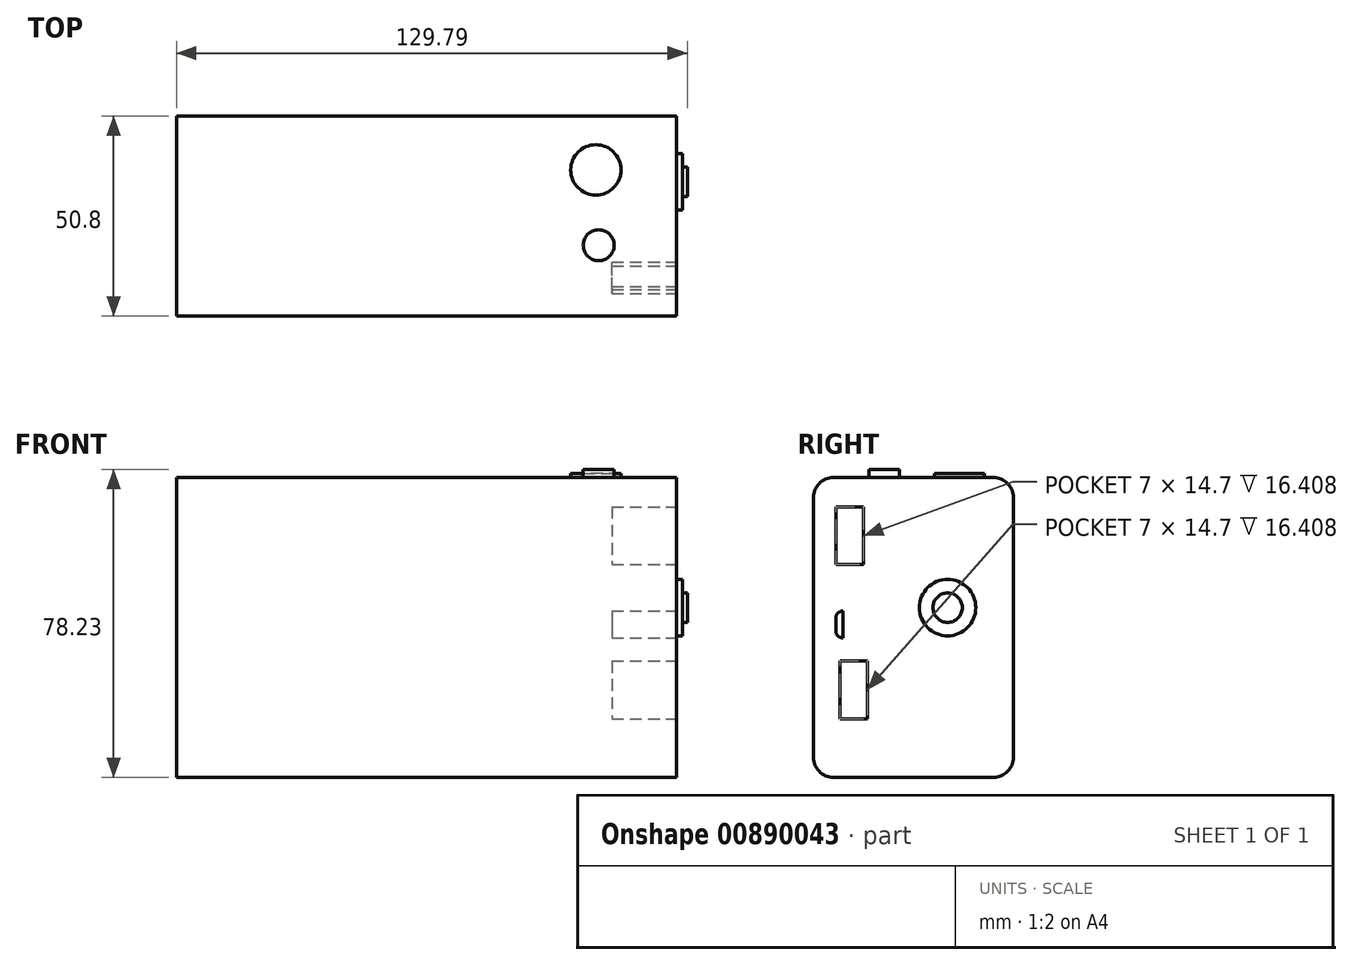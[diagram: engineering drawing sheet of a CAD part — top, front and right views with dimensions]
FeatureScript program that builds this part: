
annotation { "Feature Type Name" : "Feature", "Feature Type Description" : "" }
export const myFeature = defineFeature(function(context is Context, id is Id, definition is map)
    precondition{}
    {
        {
            var Q0;
            Q0=qCreatedBy(makeId("Front.planeOp"),FACE);
            var sketch = newSketch(context, id + "F0", { "sketchPlane" : qUnion([Q0])});
            skLineSegment(sketch, "E0.bottom", {"start": v(63.5, 38.1) * mm, "end": v(-63.5, 38.1) * mm});
            skLineSegment(sketch, "E0.top", {"start": v(63.5, -38.1) * mm, "end": v(-63.5, -38.1) * mm});
            skLineSegment(sketch, "E0.left", {"start": v(63.5, 38.1) * mm, "end": v(63.5, -38.1) * mm});
            skLineSegment(sketch, "E0.right", {"start": v(-63.5, 38.1) * mm, "end": v(-63.5, -38.1) * mm});
            skPoint(sketch, "E0.middle", {"position": v(0, 0) * mm});
            skSolve(sketch);
        }
        {
            var Q0;
            Q0=makeQuery(id+"F0.imprint","IMPRINT",FACE,{"disambiguationData":[TD([[makeQuery(id+"F0.imprint","IMPRINT",EDGE,{"derivedFrom":sQuery(id+"F0.wireOp",EDGE,"E0.bottom")}),1.0]])]});
            extrude(context, id + "F1", {"entities" : qUnion([Q0]), "depth" : 50.8 * mm, "offsetDistance" : 25.4 * mm});
        }
        {
            var Q0;
            Q0=makeQuery(id+"F1.opExtrude","CAP_EDGE",EDGE,{"disambiguationData":[OSD([sQuery(id+"F0.wireOp",EDGE,"E0.bottom")])],"isStart":false});
            var Q1;
            Q1=makeQuery(id+"F1.opExtrude","CAP_EDGE",EDGE,{"disambiguationData":[OSD([sQuery(id+"F0.wireOp",EDGE,"E0.top")])],"isStart":false});
            var Q2;
            Q2=makeQuery(id+"F1.opExtrude","CAP_EDGE",EDGE,{"disambiguationData":[OSD([sQuery(id+"F0.wireOp",EDGE,"E0.bottom")])],"isStart":true});
            var Q3;
            Q3=makeQuery(id+"F1.opExtrude","CAP_EDGE",EDGE,{"disambiguationData":[OSD([sQuery(id+"F0.wireOp",EDGE,"E0.top")])],"isStart":true});
            fillet(context, id + "F2", {"entities" : qUnion([Q0, Q1, Q2, Q3]), "radius" : 5.08 * mm, "tangentPropagation" : true, "allowEdgeOverflow" : false});
        }
        {
            var Q0;
            Q0=makeQuery(id+"F1.opExtrude","SWEPT_FACE",FACE,{"disambiguationData":[OSD([sQuery(id+"F0.wireOp",EDGE,"E0.left")])]});
            var sketch = newSketch(context, id + "F3", { "sketchPlane" : qUnion([Q0])});
            skLineSegment(sketch, "E1.bottom", {"start": v(-45.09, 30.66) * mm, "end": v(-38.09, 30.66) * mm});
            skLineSegment(sketch, "E1.top", {"start": v(-45.09, 15.96) * mm, "end": v(-38.09, 15.96) * mm});
            skLineSegment(sketch, "E1.left", {"start": v(-45.09, 30.66) * mm, "end": v(-45.09, 15.96) * mm});
            skLineSegment(sketch, "E1.right", {"start": v(-38.09, 30.66) * mm, "end": v(-38.09, 15.96) * mm});
            skSolve(sketch);
        }
        {
            var Q0;
            Q0=makeQuery(id+"F3.imprint","IMPRINT",FACE,{"disambiguationData":[TD([[makeQuery(id+"F3.imprint","IMPRINT",EDGE,{"derivedFrom":sQuery(id+"F3.wireOp",EDGE,"E1.bottom")}),-1.0]])]});
            extrude(context, id + "F4", {"entities" : qUnion([Q0]), "operationType" : NewBodyOperationType.REMOVE, "oppositeDirection" : true, "depth" : 16.4 * mm, "offsetDistance" : 25.4 * mm});
        }
        {
            var Q0;
            Q0=makeQuery(id+"F1.opExtrude","SWEPT_FACE",FACE,{"disambiguationData":[OSD([sQuery(id+"F0.wireOp",EDGE,"E0.left")])]});
            var sketch = newSketch(context, id + "F5", { "sketchPlane" : qUnion([Q0])});
            skLineSegment(sketch, "E2.bottom", {"start": v(-44.08, -8.52) * mm, "end": v(-37.08, -8.52) * mm});
            skLineSegment(sketch, "E2.top", {"start": v(-44.08, -23.22) * mm, "end": v(-37.08, -23.22) * mm});
            skLineSegment(sketch, "E2.left", {"start": v(-44.08, -8.52) * mm, "end": v(-44.08, -23.22) * mm});
            skLineSegment(sketch, "E2.right", {"start": v(-37.08, -8.52) * mm, "end": v(-37.08, -23.22) * mm});
            skSolve(sketch);
        }
        {
            var Q0;
            Q0=makeQuery(id+"F5.imprint","IMPRINT",FACE,{"disambiguationData":[TD([[makeQuery(id+"F5.imprint","IMPRINT",EDGE,{"derivedFrom":sQuery(id+"F5.wireOp",EDGE,"E2.bottom")}),-1.0]])]});
            extrude(context, id + "F6", {"entities" : qUnion([Q0]), "operationType" : NewBodyOperationType.REMOVE, "oppositeDirection" : true, "depth" : 16.4 * mm, "offsetDistance" : 25.4 * mm});
        }
        {
            var Q0;
            Q0=makeQuery(id+"F1.opExtrude","SWEPT_FACE",FACE,{"disambiguationData":[OSD([sQuery(id+"F0.wireOp",EDGE,"E0.left")])]});
            var sketch = newSketch(context, id + "F7", { "sketchPlane" : qUnion([Q0])});
            skPoint(sketch, "E3.firstSnap0", {"position": v(-45.09, 23.31) * mm});
            skLineSegment(sketch, "E3.bottom", {"start": v(-43.29, 4.18) * mm, "end": v(-43.29, 4.18) * mm});
            skLineSegment(sketch, "E3.top", {"start": v(-43.29, -2.67) * mm, "end": v(-43.29, -2.67) * mm});
            skLineSegment(sketch, "E3.left", {"start": v(-45.09, 2.38) * mm, "end": v(-45.09, -0.87) * mm});
            skLineSegment(sketch, "E3.right", {"start": v(-43.29, 4.18) * mm, "end": v(-43.29, -2.67) * mm});
            skPoint(sketch, "E4.visualSharp", {"position": v(-45.09, 4.18) * mm});
            skArc(sketch, "E4.filletArc", {"start": v(-43.29, 4.18) * mm, "mid": v(-44.56, 3.65) * mm, "end": v(-45.09, 2.38) * mm});
            skPoint(sketch, "E5.visualSharp", {"position": v(-45.09, -2.67) * mm});
            skArc(sketch, "E5.filletArc", {"start": v(-45.09, -0.87) * mm, "mid": v(-44.56, -2.15) * mm, "end": v(-43.29, -2.67) * mm});
            skSolve(sketch);
        }
        {
            var Q0;
            Q0 = qSketchRegion(id + "F7", true);
            extrude(context, id + "F8", {"entities" : qUnion([Q0]), "operationType" : NewBodyOperationType.REMOVE, "oppositeDirection" : true, "depth" : 16.4 * mm, "offsetDistance" : 25.4 * mm});
        }
        {
            var Q0;
            Q0=makeQuery(id+"F1.opExtrude","SWEPT_FACE",FACE,{"disambiguationData":[OSD([sQuery(id+"F0.wireOp",EDGE,"E0.bottom")])]});
            var sketch = newSketch(context, id + "F9", { "sketchPlane" : qUnion([Q0])});
            skCircle(sketch, "E6", {"center": v(43.03, -13.67) * mm, "radius": 6.4 * mm});
            skSolve(sketch);
        }
        {
            var Q0;
            Q0=makeQuery(id+"F9.imprint","IMPRINT",FACE,{"disambiguationData":[TD([[makeQuery(id+"F9.imprint","IMPRINT",EDGE,{"derivedFrom":sQuery(id+"F9.wireOp",EDGE,"E6")}),1.0]])]});
            extrude(context, id + "F10", {"entities" : qUnion([Q0]), "operationType" : NewBodyOperationType.ADD, "depth" : 1.02 * mm, "offsetDistance" : 25.4 * mm});
        }
        {
            var Q0;
            Q0=makeQuery(id+"F1.opExtrude","SWEPT_FACE",FACE,{"disambiguationData":[OSD([sQuery(id+"F0.wireOp",EDGE,"E0.left")])]});
            var sketch = newSketch(context, id + "F11", { "sketchPlane" : qUnion([Q0])});
            skCircle(sketch, "E7", {"center": v(-16.7, 5.04) * mm, "radius": 7.17 * mm});
            skSolve(sketch);
        }
        {
            var Q0;
            Q0=makeQuery(id+"F11.imprint","IMPRINT",FACE,{"disambiguationData":[TD([[makeQuery(id+"F11.imprint","IMPRINT",EDGE,{"derivedFrom":sQuery(id+"F11.wireOp",EDGE,"E7")}),1.0]])]});
            extrude(context, id + "F12", {"entities" : qUnion([Q0]), "operationType" : NewBodyOperationType.ADD, "depth" : 1.52 * mm, "offsetDistance" : 25.4 * mm});
        }
        {
            var Q0;
            Q0=makeQuery(id+"F12.opExtrude","CAP_FACE",FACE,{"disambiguationData":[OSD([sQuery(id+"F11.wireOp",EDGE,"E7")])],"isStart":false});
            var sketch = newSketch(context, id + "F13", { "sketchPlane" : qUnion([Q0])});
            skCircle(sketch, "E8", {"center": v(-16.7, 5.04) * mm, "radius": 3.74 * mm});
            skSolve(sketch);
        }
        {
            var Q0;
            Q0=makeQuery(id+"F13.imprint","IMPRINT",FACE,{"disambiguationData":[TD([[makeQuery(id+"F13.imprint","IMPRINT",EDGE,{"derivedFrom":sQuery(id+"F13.wireOp",EDGE,"E8")}),1.0]])]});
            extrude(context, id + "F14", {"entities" : qUnion([Q0]), "operationType" : NewBodyOperationType.ADD, "depth" : 1.27 * mm, "offsetDistance" : 25.4 * mm});
        }
        {
            var Q0;
            Q0=makeQuery(id+"F1.opExtrude","SWEPT_FACE",FACE,{"disambiguationData":[OSD([sQuery(id+"F0.wireOp",EDGE,"E0.bottom")])]});
            var sketch = newSketch(context, id + "F15", { "sketchPlane" : qUnion([Q0])});
            skCircle(sketch, "E9", {"center": v(43.75, -32.8) * mm, "radius": 3.93 * mm});
            skSolve(sketch);
        }
        {
            var Q0;
            Q0=makeQuery(id+"F15.imprint","IMPRINT",FACE,{"disambiguationData":[TD([[makeQuery(id+"F15.imprint","IMPRINT",EDGE,{"derivedFrom":sQuery(id+"F15.wireOp",EDGE,"E9")}),1.0]])]});
            extrude(context, id + "F16", {"entities" : qUnion([Q0]), "operationType" : NewBodyOperationType.ADD, "depth" : 2.03 * mm, "offsetDistance" : 25.4 * mm});
        }
    });
